# Revit family: IS_CeramixBlue_A5647_BIM_DE
name_source: partatom
category: Plumbing Fixtures
revit_build: Autodesk Revit MEP 2016 (Build: 20161004_0715(x64)
units: mm (PartAtom-declared; Revit-internal decimal feet)

## family parameters
Always vertical = No
Cut with Voids When Loaded = No
OmniClass Number = 23.45.55.17
OmniClass Title = Mixing Faucets
Part Type = Normal
Room Calculation Point = No
Round Connector Dimension = Use Diameter
Shared = No
Work Plane-Based = No

## types (1)
- A5647AA CERAMIX BLUE single lever one hole basin mixer, no pop-up waste
    Accessories = www.idealstandard.de\ersatzteile
    AssetType = Fixed
    BIMObjectName = ISI_IdealStandard_WashbasinTaps_CERAMIXBLUE_A5647AA
    BIMobject category = Basins
    BOSUseNativeGeometries = 1
    BarCode = 4015413326292
    Brand = Ideal Standard
    Brand url = http://www.idealstandard.de
    CodePerformance = 0
    Color = Chrome
    ConnectionType = Plumbing
    Cost = 0 $
    CurrencyUnit = €
    CurrentRevision = 1
    Description = A5647AA CERAMIX BLUE single lever one hole basin mixer, no pop-up waste
    DurationUnit = Jaar
    EAN code = https://4015413326292
    Edition number = 1
    ExpectedLife = 25
    FaucetFunction = mixed
    FaucetOperation = leverhandle
    FaucetType = pillar
    Features = CERAMIX BLUE single lever one hole basin mixer, no pop-up waste
    Finish = Chrome
    IFC Classification = Sanitary Terminal
    IfcExportAs = Sanitary terminal type
    IfcExportType = BRASSWARE BASIN
    Installation instructions = http://www.idealstandard.de
    InstallationInstructions = www.idealstandard.de\produkte
    LinearUnits = millimetres
    MainColor = Chrome
    MaintenanceInformation = www.idealstandard.de
    Manufacturer = http://www.idealstandard.de
    Manufacturer name = Ideal Standard
    ManufacturerURL = http://www.idealstandard.de
    Material = Brass
    Material main = Brass
    Model = A5647AA
    ModelNumber = A5647AA
    ModelReference = A5647AA CERAMIX BLUE single lever one hole basin mixer, no pop-up waste
    Name = ISI_IdealStandard_WashbasinTaps_CERAMIXBLUE_A5647AA
    NettWeight = 1,67 kg
    Nominal height = 0
    Nominal width = 0
    NominalHeight = 153 mm
    NominalLength = 181 mm
    NominalWidth = 55 mm
    Product Guid = 11bfe4fb-a808-467b-87ad-fcb7d0e79849
    Product SKU = A5647
    Product certification = 0
    Product data url = https://bimobject.com
    Product family = CERAMIX BLUE
    Product group = Basin Mixer
    Product name = CERAMIX BLUE single lever one hole basin mixer, no pop-up waste
    Product url = http://www.idealstandard.de
    ProductInformation = www.idealstandard.de/produkte
    QR code = http://bimobject.com
    Shape = Sculptured
    Size = 55x181x153 mm
    Space = Internal
    SpareParts = www.idealstandard.de/ersatzteile
    Technical description = http://www.idealstandard.de
    TestPressure = 10 Bar
    URL = http://www.idealstandard.de
    Uniclass2015Code = Pr_40_20_87_98
    Uniclass2015Title = Washbasin taps
    Uniclass2015Version = Products v1.1
    ValveMechanism = ceramic disc
    ValveOperation = lever
    VolumeUnits = Litres
    Weight Net (Kg) = 1.67
    WorkingPressure = 1-5 Bar

## geometry (parser evidence)
native form markers: Blend x4, Sweep x1
no freeform markers — native parametric forms only
